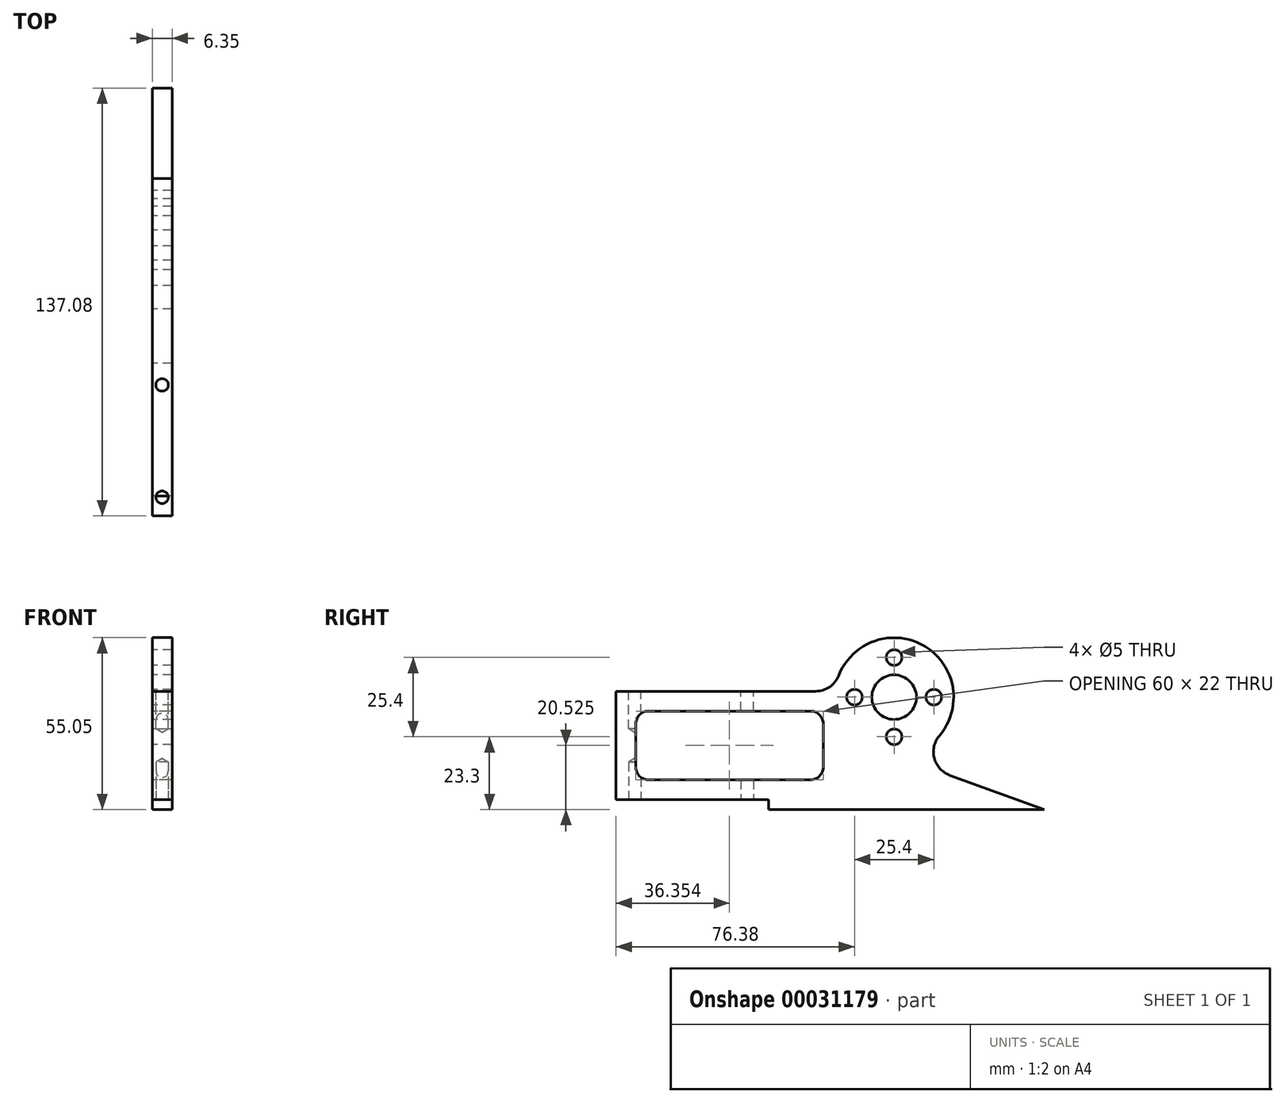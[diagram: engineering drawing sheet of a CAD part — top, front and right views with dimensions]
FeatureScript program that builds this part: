
annotation { "Feature Type Name" : "Feature", "Feature Type Description" : "" }
export const myFeature = defineFeature(function(context is Context, id is Id, definition is map)
    precondition{}
    {
        {
            var Q0;
            Q0=qCreatedBy(makeId("Right.planeOp"),FACE);
            var sketch = newSketch(context, id + "F0", { "sketchPlane" : qUnion([Q0])});
            skArc(sketch, "E0", {"start": v(14.52, -12.34) * mm, "mid": v(9.78, 16.35) * mm, "end": v(-17.74, 6.95) * mm});
            skCircle(sketch, "E1", {"center": v(0, 0) * mm, "radius": 7.14 * mm});
            skCircle(sketch, "E2", {"center": v(0, 0) * mm, "radius": 12.7 * mm, "construction": true});
            skLineSegment(sketch, "E3", {"start": v(-127.08, -32.83) * mm, "end": v(-40.2, -32.83) * mm});
            skLineSegment(sketch, "E4", {"start": v(48, -36) * mm, "end": v(17.88, -25.04) * mm});
            skLineSegment(sketch, "E5", {"start": v(-127.08, -32.83) * mm, "end": v(-127.08, -26.48) * mm});
            skLineSegment(sketch, "E6", {"start": v(-127.08, -26.48) * mm, "end": v(-93.08, -26.47) * mm});
            skLineSegment(sketch, "E7", {"start": v(-89.08, -22.47) * mm, "end": v(-89.08, -8.47) * mm});
            skLineSegment(sketch, "E8", {"start": v(-93.08, -4.47) * mm, "end": v(-127.08, -4.48) * mm});
            skLineSegment(sketch, "E9", {"start": v(-127.08, -4.48) * mm, "end": v(-127.08, 1.88) * mm});
            skLineSegment(sketch, "E10", {"start": v(-127.08, 1.88) * mm, "end": v(-25.18, 1.88) * mm});
            skPoint(sketch, "E11.visualSharp", {"position": v(-89.08, -4.47) * mm});
            skArc(sketch, "E11.filletArc", {"start": v(-89.08, -8.47) * mm, "mid": v(-90.25, -5.65) * mm, "end": v(-93.08, -4.47) * mm});
            skPoint(sketch, "E12.visualSharp", {"position": v(-89.08, -26.47) * mm});
            skArc(sketch, "E12.filletArc", {"start": v(-93.08, -26.47) * mm, "mid": v(-90.25, -25.3) * mm, "end": v(-89.08, -22.47) * mm});
            skPoint(sketch, "E13.visualSharp", {"position": v(-18.96, 1.88) * mm});
            skArc(sketch, "E13.filletArc", {"start": v(-25.18, 1.88) * mm, "mid": v(-20.68, 3.27) * mm, "end": v(-17.74, 6.95) * mm});
            skPoint(sketch, "E14.visualSharp", {"position": v(1.3, -19) * mm});
            skArc(sketch, "E14.filletArc", {"start": v(14.52, -12.34) * mm, "mid": v(12.88, -19.56) * mm, "end": v(17.88, -25.04) * mm});
            skCircle(sketch, "E15", {"center": v(0, 12.7) * mm, "radius": 2.5 * mm});
            skCircle(sketch, "E16", {"center": v(-12.7, 0) * mm, "radius": 2.5 * mm});
            skCircle(sketch, "E17", {"center": v(12.7, 0) * mm, "radius": 2.5 * mm});
            skCircle(sketch, "E18", {"center": v(0, -12.7) * mm, "radius": 2.5 * mm});
            skLineSegment(sketch, "E19.bottom", {"start": v(-78.73, -4.47) * mm, "end": v(-26.73, -4.47) * mm});
            skLineSegment(sketch, "E19.left", {"start": v(-82.73, -8.47) * mm, "end": v(-82.73, -22.47) * mm});
            skLineSegment(sketch, "E19.right", {"start": v(-22.73, -8.47) * mm, "end": v(-22.73, -22.47) * mm});
            skPoint(sketch, "E20.visualSharp", {"position": v(-82.73, -4.47) * mm});
            skArc(sketch, "E20.filletArc", {"start": v(-78.73, -4.47) * mm, "mid": v(-81.55, -5.65) * mm, "end": v(-82.73, -8.47) * mm});
            skArc(sketch, "E21.filletArc", {"start": v(-82.73, -22.47) * mm, "mid": v(-81.55, -25.3) * mm, "end": v(-78.73, -26.47) * mm});
            skPoint(sketch, "E22.visualSharp", {"position": v(-22.73, -4.47) * mm});
            skArc(sketch, "E22.filletArc", {"start": v(-22.73, -8.47) * mm, "mid": v(-23.9, -5.65) * mm, "end": v(-26.73, -4.47) * mm});
            skLineSegment(sketch, "E23", {"start": v(-40.2, -32.83) * mm, "end": v(-40.2, -36) * mm});
            skLineSegment(sketch, "E24", {"start": v(-40.2, -36) * mm, "end": v(48, -36) * mm});
            skArc(sketch, "E25.filletArc", {"start": v(-26.73, -26.47) * mm, "mid": v(-23.9, -25.3) * mm, "end": v(-22.73, -22.47) * mm});
            skLineSegment(sketch, "E26", {"start": v(-78.73, -26.47) * mm, "end": v(-26.73, -26.47) * mm});
            skSolve(sketch);
        }
        {
            var Q0;
            Q0 = qSketchRegion(id + "F0", true);
            extrude(context, id + "F1", {"entities" : qUnion([Q0]), "depth" : 6.35 * mm});
        }
        {
            var Q0;
            Q0=makeQuery(id+"F1.opExtrude","SWEPT_FACE",FACE,{"disambiguationData":[OSD([sQuery(id+"F0.wireOp",EDGE,"E10")])]});
            var sketch = newSketch(context, id + "F2", { "sketchPlane" : qUnion([Q0])});
            skLineSegment(sketch, "E27.bottom", {"start": v(0, -127.08) * mm, "end": v(6.35, -127.08) * mm});
            skLineSegment(sketch, "E27.top", {"start": v(0, -89.08) * mm, "end": v(6.35, -89.08) * mm});
            skLineSegment(sketch, "E27.left", {"start": v(0, -127.08) * mm, "end": v(0, -89.08) * mm});
            skLineSegment(sketch, "E27.right", {"start": v(6.35, -127.08) * mm, "end": v(6.35, -89.08) * mm});
            skSolve(sketch);
        }
        {
            var Q0;
            Q0 = qSketchRegion(id + "F2", true);
            extrude(context, id + "F3", {"entities" : qUnion([Q0]), "operationType" : NewBodyOperationType.REMOVE, "endBound" : BoundingType.THROUGH_ALL, "oppositeDirection" : true, "depth" : 25 * mm});
        }
        {
            var Q0;
            Q0=makeQuery(id+"F1.opExtrude","SWEPT_FACE",FACE,{"disambiguationData":[OSD([sQuery(id+"F0.wireOp",EDGE,"E10")])]});
            var sketch = newSketch(context, id + "F4", { "sketchPlane" : qUnion([Q0])});
            skPoint(sketch, "E28", {"position": v(3.18, -83.08) * mm});
            skPoint(sketch, "E29", {"position": v(3.17, -47.08) * mm});
            skLineSegment(sketch, "E30", {"start": v(3.17, -89.08) * mm, "end": v(3.17, -83.08) * mm, "construction": true});
            skLineSegment(sketch, "E31", {"start": v(3.17, -47.08) * mm, "end": v(3.18, -83.08) * mm, "construction": true});
            skSolve(sketch);
        }
        {
            var Q0;
            Q0=sQuery(id+"F4.wireOp",VERTEX,"E28");
            var Q1;
            Q1=sQuery(id+"F4.wireOp",VERTEX,"E29");
            var Q2;
            Q2=makeQuery(id+"F1.opExtrude","SWEPT_BODY",BODY,{"disambiguationData":[OSD([sQuery(id+"F0.wireOp",EDGE,"E0"),sQuery(id+"F0.wireOp",EDGE,"E1"),sQuery(id+"F0.wireOp",EDGE,"E3"),sQuery(id+"F0.wireOp",EDGE,"E4"),sQuery(id+"F0.wireOp",EDGE,"E5"),sQuery(id+"F0.wireOp",EDGE,"E6"),sQuery(id+"F0.wireOp",EDGE,"E7"),sQuery(id+"F0.wireOp",EDGE,"E8"),sQuery(id+"F0.wireOp",EDGE,"E9"),sQuery(id+"F0.wireOp",EDGE,"E10"),sQuery(id+"F0.wireOp",EDGE,"E11.filletArc"),sQuery(id+"F0.wireOp",EDGE,"E12.filletArc"),sQuery(id+"F0.wireOp",EDGE,"E13.filletArc"),sQuery(id+"F0.wireOp",EDGE,"E14.filletArc"),sQuery(id+"F0.wireOp",EDGE,"E15"),sQuery(id+"F0.wireOp",EDGE,"E16"),sQuery(id+"F0.wireOp",EDGE,"E17"),sQuery(id+"F0.wireOp",EDGE,"E18"),sQuery(id+"F0.wireOp",EDGE,"E19.bottom"),sQuery(id+"F0.wireOp",EDGE,"E19.left"),sQuery(id+"F0.wireOp",EDGE,"E19.right"),sQuery(id+"F0.wireOp",EDGE,"E20.filletArc"),sQuery(id+"F0.wireOp",EDGE,"E21.filletArc"),sQuery(id+"F0.wireOp",EDGE,"E22.filletArc"),sQuery(id+"F0.wireOp",EDGE,"E23"),sQuery(id+"F0.wireOp",EDGE,"E24"),sQuery(id+"F0.wireOp",EDGE,"E25.filletArc"),sQuery(id+"F0.wireOp",EDGE,"E26")])]});
            hole(context, id + "F5", {"style" : HoleStyle.SIMPLE, "holeDiameter" : 4 * mm, "endStyle" : HoleEndStyle.BLIND, "holeDepth" : 12 * mm, "locations" : qUnion([Q0, Q1]), "scope" : qUnion([Q2])});
        }
        {
            var Q0;
            Q0=makeQuery(id+"F1.opExtrude","SWEPT_FACE",FACE,{"disambiguationData":[OSD([sQuery(id+"F0.wireOp",EDGE,"E3")])]});
            var sketch = newSketch(context, id + "F6", { "sketchPlane" : qUnion([Q0])});
            skPoint(sketch, "E32", {"position": v(3.18, 83.08) * mm});
            skPoint(sketch, "E33", {"position": v(3.18, 47.08) * mm});
            skLineSegment(sketch, "E34", {"start": v(3.18, 89.08) * mm, "end": v(3.18, 83.08) * mm, "construction": true});
            skLineSegment(sketch, "E35", {"start": v(3.18, 47.08) * mm, "end": v(3.18, 83.08) * mm, "construction": true});
            skSolve(sketch);
        }
        {
            var Q0;
            Q0=sQuery(id+"F6.wireOp",VERTEX,"E34.end");
            var Q1;
            Q1=sQuery(id+"F6.wireOp",VERTEX,"E35.start");
            var Q2;
            Q2=makeQuery(id+"F1.opExtrude","SWEPT_BODY",BODY,{"disambiguationData":[OSD([sQuery(id+"F0.wireOp",EDGE,"E0"),sQuery(id+"F0.wireOp",EDGE,"E1"),sQuery(id+"F0.wireOp",EDGE,"E3"),sQuery(id+"F0.wireOp",EDGE,"E4"),sQuery(id+"F0.wireOp",EDGE,"E5"),sQuery(id+"F0.wireOp",EDGE,"E6"),sQuery(id+"F0.wireOp",EDGE,"E7"),sQuery(id+"F0.wireOp",EDGE,"E8"),sQuery(id+"F0.wireOp",EDGE,"E9"),sQuery(id+"F0.wireOp",EDGE,"E10"),sQuery(id+"F0.wireOp",EDGE,"E11.filletArc"),sQuery(id+"F0.wireOp",EDGE,"E12.filletArc"),sQuery(id+"F0.wireOp",EDGE,"E13.filletArc"),sQuery(id+"F0.wireOp",EDGE,"E14.filletArc"),sQuery(id+"F0.wireOp",EDGE,"E15"),sQuery(id+"F0.wireOp",EDGE,"E16"),sQuery(id+"F0.wireOp",EDGE,"E17"),sQuery(id+"F0.wireOp",EDGE,"E18"),sQuery(id+"F0.wireOp",EDGE,"E19.bottom"),sQuery(id+"F0.wireOp",EDGE,"E19.left"),sQuery(id+"F0.wireOp",EDGE,"E19.right"),sQuery(id+"F0.wireOp",EDGE,"E20.filletArc"),sQuery(id+"F0.wireOp",EDGE,"E21.filletArc"),sQuery(id+"F0.wireOp",EDGE,"E22.filletArc"),sQuery(id+"F0.wireOp",EDGE,"E23"),sQuery(id+"F0.wireOp",EDGE,"E24"),sQuery(id+"F0.wireOp",EDGE,"E25.filletArc"),sQuery(id+"F0.wireOp",EDGE,"E26")])]});
            hole(context, id + "F7", {"style" : HoleStyle.SIMPLE, "holeDiameter" : 4 * mm, "endStyle" : HoleEndStyle.BLIND, "holeDepth" : 12 * mm, "locations" : qUnion([Q0, Q1]), "scope" : qUnion([Q2])});
        }
    });
